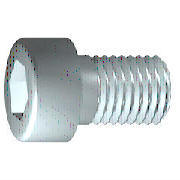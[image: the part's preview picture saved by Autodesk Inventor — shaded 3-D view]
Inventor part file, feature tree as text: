
AUTODESK INVENTOR PART (.ipt)
format: ipt  version: 2013 (Build 170138000, 138)  size: 185,344 bytes
history: native  units: mm (DEFAULTED — no unit token found)
features: sketch x2, extrude x1, plane x1, fillet x1
ambient origin geometry x7: Origin, YZ Plane, XY Plane, X Axis, Y Axis, Z Axis, Center Point
bodies: Solid1 (feature_tree), Body (feature_tree)
feature tree (5):
  extrude  "Slot"  Depth=0.306825mm
  plane  "Work Plane1"
  fillet  "Fillet2"  Radius=3.0mm
  sketch  "Sketch1"  dims[d1=14.693275mm d2=0.306825mm d3=3.0mm]
  sketch  "Sketch2"  dims[d4=1.5mm d5=60.0deg d6=3.0mm d7=3.0mm d8=2.886751mm d9=5.5mm d10=90.0deg d11=10.0mm d12=0.0mm d13=14.693275mm d14=0.0mm d15=0.306725mm d16=0.306725mm d17=0.3mm d19=0.0mm d26=16.0mm d27=45.0deg d28=0.0mm d29=0.0mm d30=0.1mm]
